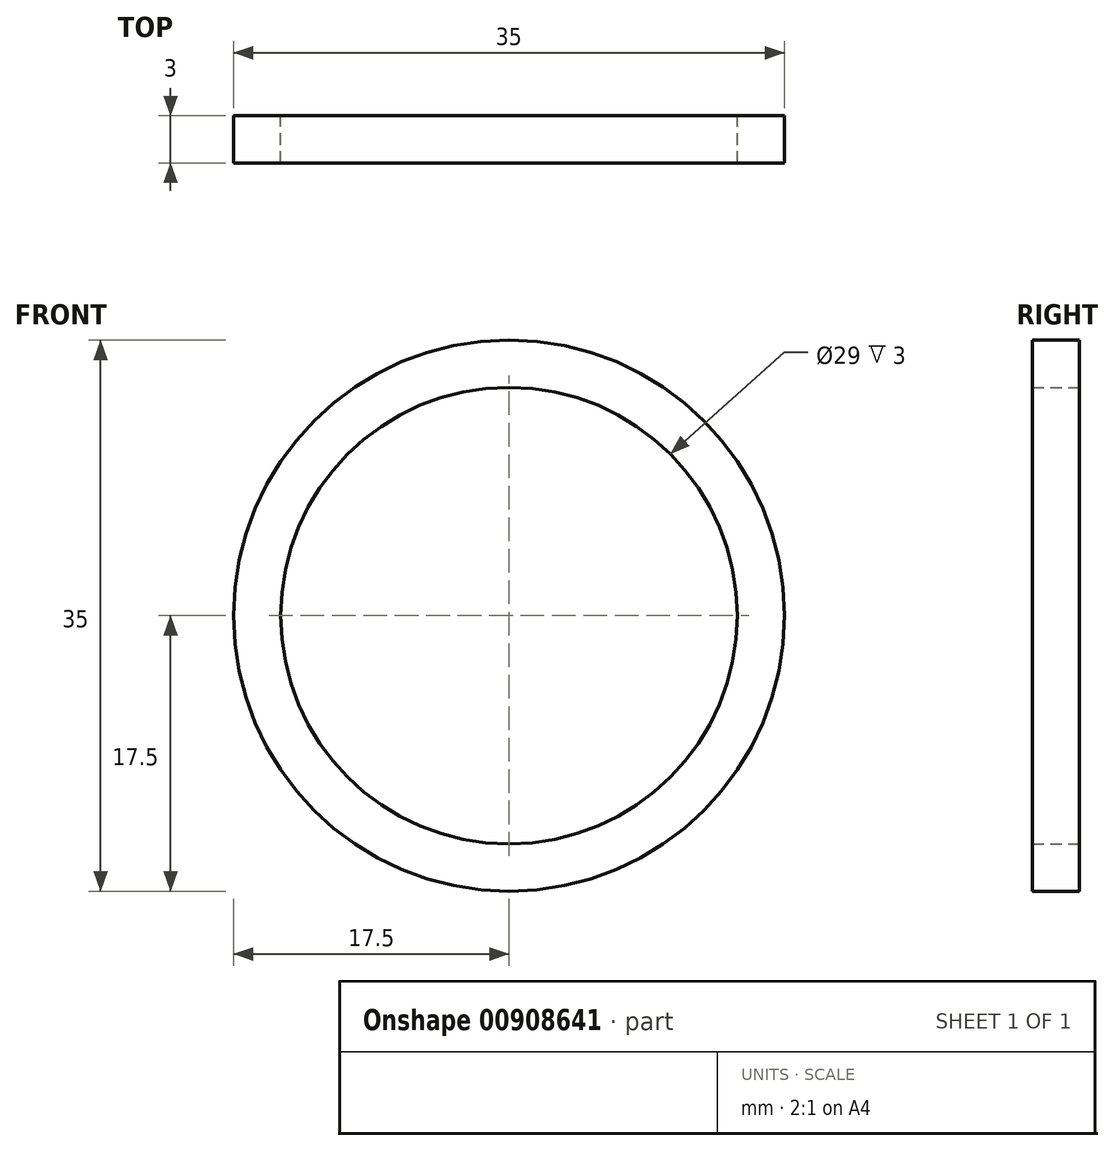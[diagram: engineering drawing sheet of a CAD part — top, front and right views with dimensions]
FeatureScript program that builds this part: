
annotation { "Feature Type Name" : "Feature", "Feature Type Description" : "" }
export const myFeature = defineFeature(function(context is Context, id is Id, definition is map)
    precondition{}
    {
        {
            var Q0;
            Q0=qCreatedBy(makeId("Front.planeOp"),FACE);
            var sketch = newSketch(context, id + "F0", { "sketchPlane" : qUnion([Q0])});
            skCircle(sketch, "E0", {"center": v(0, 0) * mm, "radius": 14.5 * mm});
            skCircle(sketch, "E1", {"center": v(0, 0) * mm, "radius": 17.5 * mm});
            skSolve(sketch);
        }
        {
            var Q0;
            Q0=makeQuery(id+"F0.imprint","IMPRINT",FACE,{"disambiguationData":[TD([[makeQuery(id+"F0.imprint","IMPRINT",EDGE,{"derivedFrom":sQuery(id+"F0.wireOp",EDGE,"E0")}),-1.0]])]});
            extrude(context, id + "F1", {"entities" : qUnion([Q0]), "depth" : 3 * mm, "offsetDistance" : 25 * mm});
        }
    });
